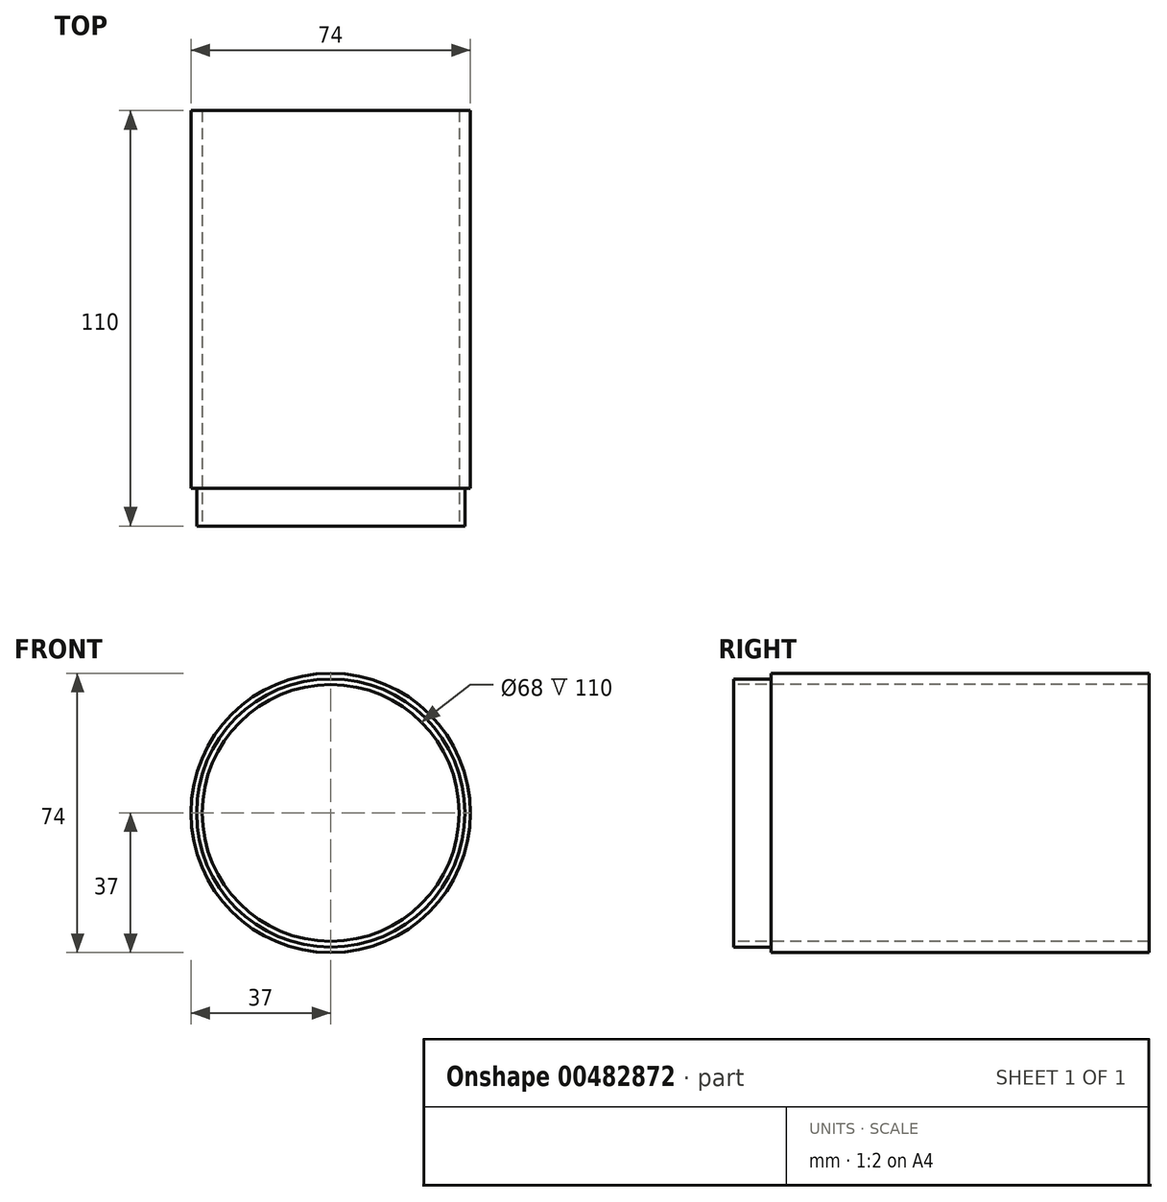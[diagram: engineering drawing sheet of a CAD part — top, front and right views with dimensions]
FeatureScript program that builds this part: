
annotation { "Feature Type Name" : "Feature", "Feature Type Description" : "" }
export const myFeature = defineFeature(function(context is Context, id is Id, definition is map)
    precondition{}
    {
        {
            var Q0;
            Q0=qCreatedBy(makeId("Front.planeOp"),FACE);
            var sketch = newSketch(context, id + "F0", { "sketchPlane" : qUnion([Q0])});
            skCircle(sketch, "E0", {"center": v(0, 0) * mm, "radius": 37 * mm});
            skCircle(sketch, "E1", {"center": v(0, 0) * mm, "radius": 34 * mm});
            skSolve(sketch);
        }
        {
            var Q0;
            Q0 = qSketchRegion(id + "F0", true);
            extrude(context, id + "F1", {"entities" : qUnion([Q0]), "oppositeDirection" : true, "depth" : 100 * mm});
        }
        {
            var Q0;
            Q0=qCreatedBy(makeId("Front.planeOp"),FACE);
            var sketch = newSketch(context, id + "F2", { "sketchPlane" : qUnion([Q0])});
            skCircle(sketch, "E2", {"center": v(0, 0) * mm, "radius": 35.5 * mm});
            skSolve(sketch);
        }
        {
            var Q0;
            Q0=makeQuery(id+"F2.imprint","IMPRINT",FACE,{"disambiguationData":[TD([[makeQuery(id+"F2.imprint","IMPRINT",EDGE,{"derivedFrom":sQuery(id+"F2.wireOp",EDGE,"E2")}),1.0]])]});
            extrude(context, id + "F3", {"entities" : qUnion([Q0]), "operationType" : NewBodyOperationType.ADD, "depth" : 10 * mm});
        }
        {
            var Q0;
            Q0=makeQuery(id+"F3.opExtrude","CAP_FACE",FACE,{"disambiguationData":[OSD([sQuery(id+"F2.wireOp",EDGE,"E2")])],"isStart":false});
            var sketch = newSketch(context, id + "F4", { "sketchPlane" : qUnion([Q0])});
            skCircle(sketch, "E3", {"center": v(0, 0) * mm, "radius": 34 * mm});
            skSolve(sketch);
        }
        {
            var Q0;
            Q0=makeQuery(id+"F4.imprint","IMPRINT",FACE,{"disambiguationData":[TD([[makeQuery(id+"F4.imprint","IMPRINT",EDGE,{"derivedFrom":sQuery(id+"F4.wireOp",EDGE,"E3")}),1.0]])]});
            extrude(context, id + "F5", {"entities" : qUnion([Q0]), "operationType" : NewBodyOperationType.REMOVE, "oppositeDirection" : true, "depth" : 25 * mm});
        }
    });
